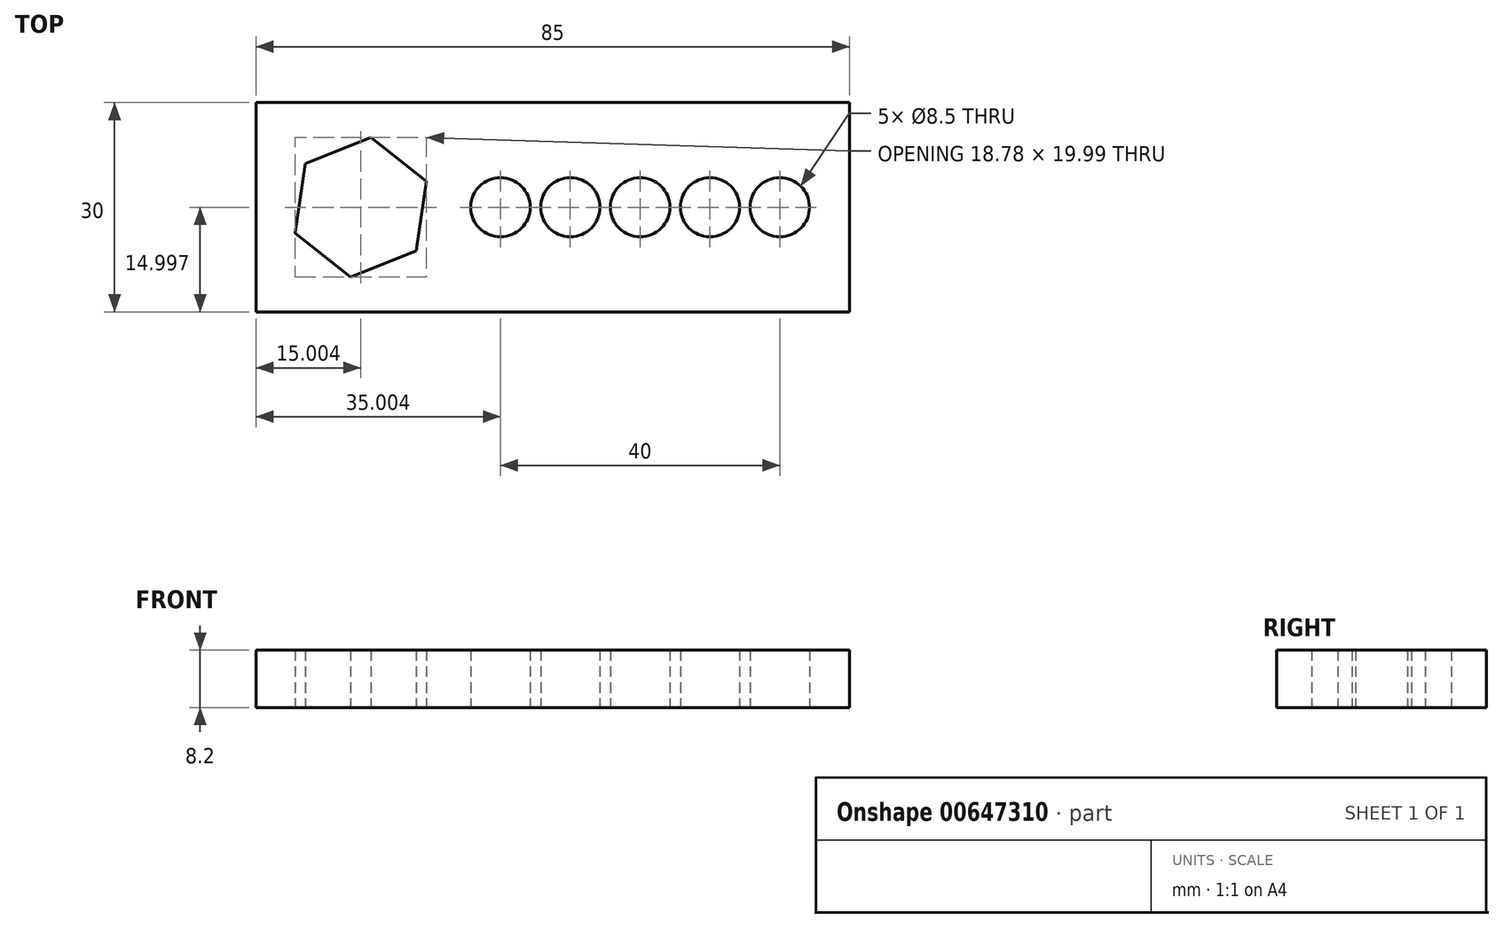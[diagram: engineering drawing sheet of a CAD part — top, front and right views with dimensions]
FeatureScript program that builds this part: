
annotation { "Feature Type Name" : "Feature", "Feature Type Description" : "" }
export const myFeature = defineFeature(function(context is Context, id is Id, definition is map)
    precondition{}
    {
        {
            var Q0;
            Q0=qCreatedBy(makeId("Top.planeOp"),FACE);
            var sketch = newSketch(context, id + "F0", { "sketchPlane" : qUnion([Q0])});
            skLineSegment(sketch, "E0.bottom", {"start": v(-40.58, 17.15) * mm, "end": v(44.42, 17.15) * mm});
            skLineSegment(sketch, "E0.top", {"start": v(-40.58, -12.85) * mm, "end": v(44.42, -12.85) * mm});
            skLineSegment(sketch, "E0.left", {"start": v(-40.58, 17.15) * mm, "end": v(-40.58, -12.85) * mm});
            skLineSegment(sketch, "E0.right", {"start": v(44.42, 17.15) * mm, "end": v(44.42, -12.85) * mm});
            skLineSegment(sketch, "E1", {"start": v(-40.58, 2.15) * mm, "end": v(44.42, 2.15) * mm, "construction": true});
            skCircle(sketch, "E2.cCircle", {"center": v(-25.58, 2.15) * mm, "radius": 8.75 * mm, "construction": true});
            skLineSegment(sketch, "E2.0", {"start": v(-33.5, 8.41) * mm, "end": v(-24.11, 12.14) * mm});
            skLineSegment(sketch, "E2.1", {"start": v(-24.11, 12.14) * mm, "end": v(-16.19, 5.88) * mm});
            skLineSegment(sketch, "E2.2", {"start": v(-16.19, 5.88) * mm, "end": v(-17.65, -4.12) * mm});
            skLineSegment(sketch, "E2.3", {"start": v(-17.65, -4.12) * mm, "end": v(-27.04, -7.85) * mm});
            skLineSegment(sketch, "E2.4", {"start": v(-27.04, -7.85) * mm, "end": v(-34.97, -1.59) * mm});
            skLineSegment(sketch, "E2.5", {"start": v(-34.97, -1.59) * mm, "end": v(-33.5, 8.41) * mm});
            skPoint(sketch, "E2.0.midPoint", {"position": v(-28.8, 10.28) * mm});
            skCircle(sketch, "E3", {"center": v(-5.58, 2.15) * mm, "radius": 4.25 * mm});
            skCircle(sketch, "E4", {"center": v(4.42, 2.15) * mm, "radius": 4.25 * mm});
            skCircle(sketch, "E5", {"center": v(14.42, 2.15) * mm, "radius": 4.25 * mm});
            skCircle(sketch, "E6", {"center": v(24.42, 2.15) * mm, "radius": 4.25 * mm});
            skCircle(sketch, "E7", {"center": v(34.42, 2.15) * mm, "radius": 4.25 * mm});
            skSolve(sketch);
        }
        {
            var Q0;
            Q0=makeQuery(id+"F0.imprint","IMPRINT",FACE,{"disambiguationData":[TD([[makeQuery(id+"F0.imprint","IMPRINT",EDGE,{"derivedFrom":sQuery(id+"F0.wireOp",EDGE,"E0.bottom")}),-1.0]])]});
            extrude(context, id + "F1", {"entities" : qUnion([Q0]), "depth" : 8.2 * mm, "offsetDistance" : 25 * mm});
        }
    });
